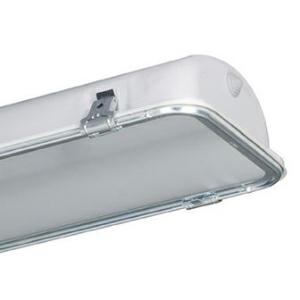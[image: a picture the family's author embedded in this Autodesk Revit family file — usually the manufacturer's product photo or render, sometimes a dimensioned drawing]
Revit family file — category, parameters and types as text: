
# Revit family: 3f_filippi_-_beta_i3f_76_vs_ampio_3f_filippi_-_55149_-_i3f_led_762x30w_ep_ampio_vs_l1565
name_source: partatom
category: Lighting Fixtures
units: mm (PartAtom-declared; Revit-internal decimal feet)

## family parameters
Cut with Voids When Loaded = No
Host = Face
Light Source = No
Part Type = Normal
Room Calculation Point = No
Round Connector Dimension = Use Diameter
Shared = No

## types (1)
- 3F Filippi - Beta i3F 76 VS Ampio (1 x LED, 8820 lm, 67 W, 4000 K)
    Apparent Load = 67 VA
    Approval mark = ENEC
    CIE Flux Codes = 62 90 98 100 100
    Color Rendering = 80
    Color Temperature = 4000 K
    Control Gear = Electronic ballast
    Default Elevation = 1800 mm
    Description = ILLUMINOTECHNICAL
Luminous efficiency 100% (DLOR 100%, ULOR 0%).
Initial luminous flux of the luminaire 8820 lm.
Emergency luminaire luminous flux BLF 5.7%.
Wide symmetric distribution.
Installation Interdistance Transv.D = 1.31 x hu - Long.D = 1.31 x hu.
Tabular UGR (CIE 117 - 4H-8H; S=0.25H; 70/50/20): RUG 19.8 - 21.1.
Beam angle: 90° - 99°.
Luminous efficacy 132 lm/W.
Lifetime (L93/B10): 30000 h. (tq+25°C)
Lifetime (L90/B10): 50000 h. (tq+25°C)
Lifetime (L85/B10): 80000 h. (tq+25°C)
Lifetime (L80/B10): 100000 h. (tq+25°C)
Sudden decreased luminous flux after 50000 hours: 0% (C0).
Photobiological safety in compliance with IEC/TR 62778: RG0 risk exempt, (IEC 62471).
In compliance with IEC/EN 62722-2-1 - IEC/EN 62717 standards.

SOURCE
2 linear LED modules 30W/840.
Energy efficiency class (UE 2019/2020 - UE 2019/2015): D.
CIE 13.3 Colour rendering index: CRI >80 (R9 <50%).
IES TM-30 Fidelity Index: Rf = 84 Rg = 95.
CCT nominal colour temperature 4000 K.
Colour initial tolerance (MacAdam): SDCM 3.

MECHANICAL
Single-piece housing in pressed steel, powder-coated in white epoxy-polyester.
Moulded anti-glare glass, non-combustible, tempered, mounted and locked to the single-piece galvanised steel perimetrical frame, sealing gasket, hinged opening by means of galvanised steel clips.
Wide flow recuperator, oversized, in specular aluminium with superficial titanium-magnesium treatment, non-iridescent.
Gear-tray unit in hot-galvanised steel, painted in white polyester, fixed to the housing by means of "Ribloc" rapid devices in galvanised steel, hinged opening.
Luminaire with limited surface temperature. - D - (EN 60598-2-24)
Dimensions: 1565x235 mm, height 105 mm. Weight 10.315 kg.
IP65 protection degree.
Mechanical strength to impacts IK09 (10 joule).
Glow-wire test resistance 960°C.

ELECTRICAL
Halogen Free electronic wiring 230V-50/60Hz, power factor 0.95, THD <25%, constant output current, SELV, class I, 1 driver.
Power of the luminaire 67 W.
CE - IEC 60598-1 - EN 60598-1.
EP maintained emergency wiring on board, 1h duration, 24h recharge; compliant with EN 60598-2-22, excluding high risk areas.
SAFE FLICKER: PstLM=<1 and SVM=<0.4 (IEC TR 61547-1 and IEC TR 63158), to ensure a more comfortable and safe light.
Ambient temperature from +5°C to +25°C.
Temperature class T6 max 85°C.
Relative humidity UR: <85%.

INSTALLATION
Ceiling / Suspended / Wall.
All accessories dedicated to this product are available on the Catalog and on our website www.3F-Filippi.com.

APPLICATIONS
In industrial environments, stores and dry, dusty indoor environments, subject to occasional water splashes.

WARNING
Fixture not suitable for cold stores with an ambient temperature <5°C and/or relative humidity >85%.
Luminaire designed for disposal/recycling at end-of-life.
Replaceable (LED only) light source by a professional. Replaceable control gear by a professional.
    Height = 105 mm
    Lamp = 1 x LED
    Lamp Light Flux = 8820 lm
    Lamp Power = 67 W
    Lamp count = 1
    Length = 1565 mm
    Lifetime = 50000 h
    Luminous efficacy = 132 lm/W
    Manufacturer = 3F Filippi
    ModVariant = No
    Model = 3F Filippi - 55149 - i3F LED 762x30W EP AMPIO VS L1565
    Mounting Place = Ceiling
    Mounting Type = Pendant
    Number of Poles = 1
    OnlyDefault = Yes
    Power Factor = 1
    Product Name = 3F Filippi - Beta i3F 76 VS Ampio
    Product group = pendant luminaire
    ProductGroupID = 9
    Protection Class = Protection class I
    Protection Degree = IP 65
    RLX_Detail_Level = 1
    RLX_Emergency_Light_Flux = 0 lm
    RLX_Emergency_Type = 0
    RLX_Emergency_Type_DB = No
    RlxData = <blob elided: 64117 chars, md5=147cbad8>
    Socket = socket
    Standby Power = 0 W
    System Light Flux = 8820 lm
    System Power = 67 W
    Type Comments = Product without accessories
    Type Image = 3ffilippi_55149.jpg
    URL = http://relux.com
    VarID = ---
    Voltage = 0 V
    Weight = 0.00 kg
    Width = 235 mm

## geometry (parser evidence)
native form markers: Blend x4, Sweep x12
no freeform markers — native parametric forms only
